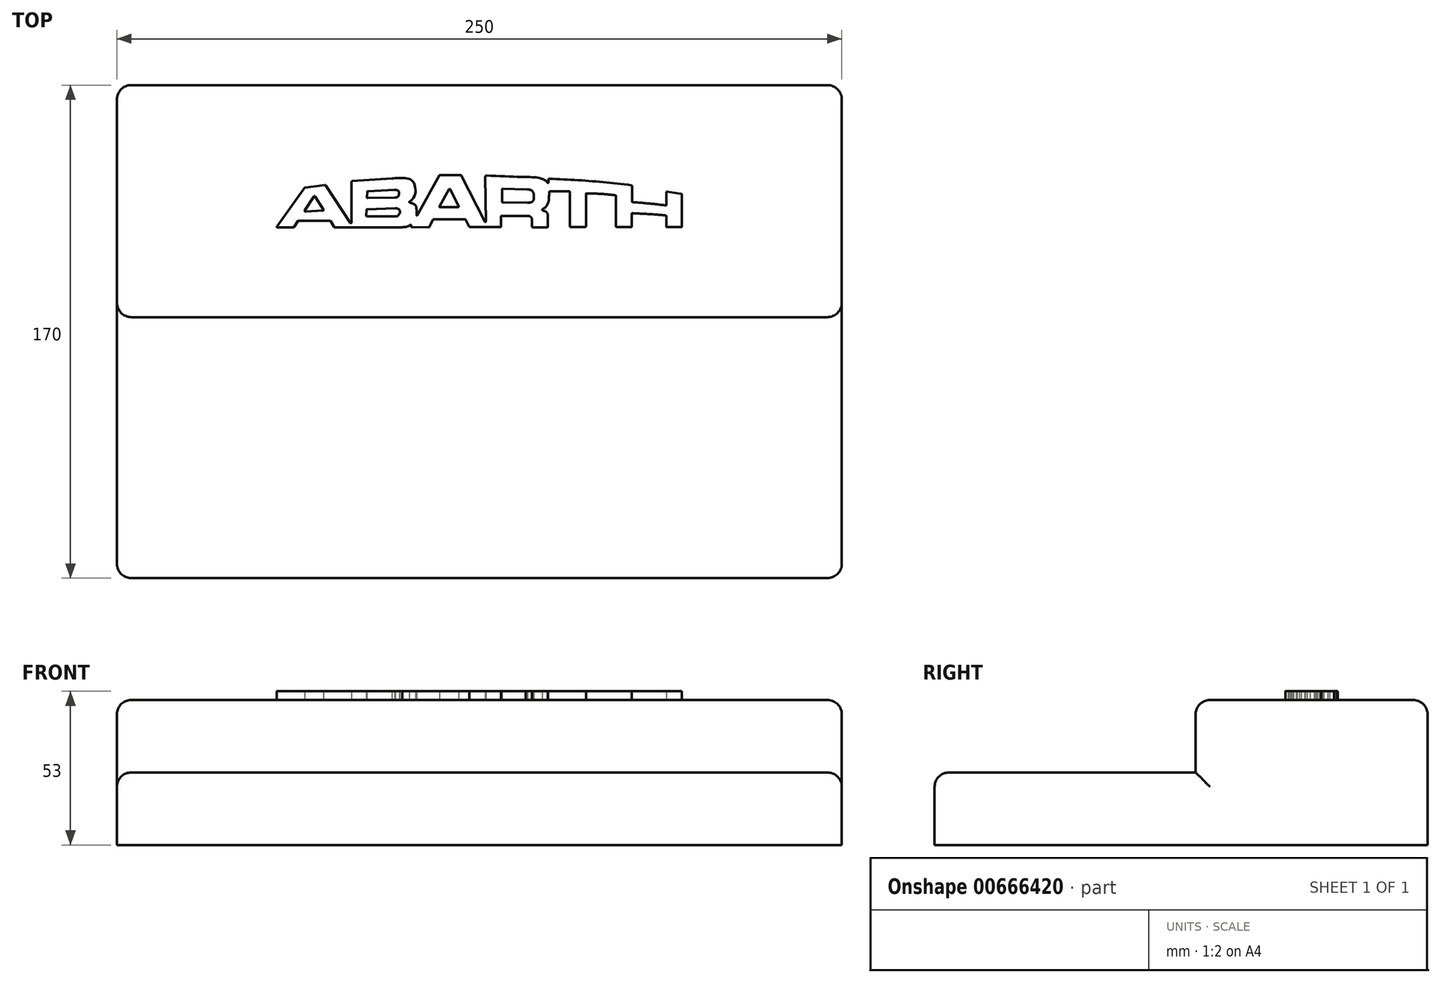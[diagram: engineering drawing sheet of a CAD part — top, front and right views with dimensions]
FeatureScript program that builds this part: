
annotation { "Feature Type Name" : "Feature", "Feature Type Description" : "" }
export const myFeature = defineFeature(function(context is Context, id is Id, definition is map)
    precondition{}
    {
        {
            var Q0;
            Q0=qCreatedBy(makeId("Top.planeOp"),FACE);
            var sketch = newSketch(context, id + "F0", { "sketchPlane" : qUnion([Q0])});
            skLineSegment(sketch, "E0.bottom", {"start": v(125, -40) * mm, "end": v(-125, -40) * mm});
            skLineSegment(sketch, "E0.top", {"start": v(125, 40) * mm, "end": v(-125, 40) * mm});
            skLineSegment(sketch, "E0.left", {"start": v(125, -40) * mm, "end": v(125, 40) * mm});
            skLineSegment(sketch, "E0.right", {"start": v(-125, -40) * mm, "end": v(-125, 40) * mm});
            skPoint(sketch, "E0.middle", {"position": v(0, 0) * mm});
            skSolve(sketch);
        }
        {
            var Q0;
            Q0=makeQuery(id+"F0.imprint","IMPRINT",FACE,{"disambiguationData":[TD([[makeQuery(id+"F0.imprint","IMPRINT",EDGE,{"derivedFrom":sQuery(id+"F0.wireOp",EDGE,"E0.bottom")}),-1.0]])]});
            extrude(context, id + "F1", {"entities" : qUnion([Q0]), "depth" : 25 * mm, "offsetDistance" : 25 * mm});
        }
        {
            var Q0;
            Q0=makeQuery(id+"F1.opExtrude","CAP_FACE",FACE,{"disambiguationData":[OSD([sQuery(id+"F0.wireOp",EDGE,"E0.bottom"),sQuery(id+"F0.wireOp",EDGE,"E0.top"),sQuery(id+"F0.wireOp",EDGE,"E0.left"),sQuery(id+"F0.wireOp",EDGE,"E0.right")])],"isStart":false});
            var sketch = newSketch(context, id + "F2", { "sketchPlane" : qUnion([Q0])});
            skLineSegment(sketch, "E1", {"start": v(-69.64, -9.06) * mm, "end": v(-64.06, -9.06) * mm});
            skLineSegment(sketch, "E2", {"start": v(-63.89, -8.97) * mm, "end": v(-62.5, -6.84) * mm});
            skLineSegment(sketch, "E3", {"start": v(-62.33, -6.75) * mm, "end": v(-51.48, -6.75) * mm});
            skLineSegment(sketch, "E4", {"start": v(-51.3, -6.84) * mm, "end": v(-50.02, -8.94) * mm});
            skLineSegment(sketch, "E5", {"start": v(-49.85, -9.04) * mm, "end": v(-26.5, -9) * mm});
            skLineSegment(sketch, "E6", {"start": v(-23.3, -8.96) * mm, "end": v(-17.46, -9.05) * mm});
            skLineSegment(sketch, "E7", {"start": v(-17.28, -8.95) * mm, "end": v(-15.84, -6.3) * mm});
            skLineSegment(sketch, "E8", {"start": v(-15.75, -6.24) * mm, "end": v(-4.93, -6.24) * mm});
            skLineSegment(sketch, "E9", {"start": v(-4.75, -6.35) * mm, "end": v(-3.41, -9) * mm});
            skLineSegment(sketch, "E10", {"start": v(-3.41, -9) * mm, "end": v(7.3, -8.99) * mm});
            skLineSegment(sketch, "E11", {"start": v(7.5, -8.79) * mm, "end": v(7.49, -5.27) * mm});
            skLineSegment(sketch, "E12", {"start": v(7.69, -5.07) * mm, "end": v(15.94, -5.07) * mm});
            skLineSegment(sketch, "E13", {"start": v(18.18, -6.73) * mm, "end": v(18.18, -8.82) * mm});
            skLineSegment(sketch, "E14", {"start": v(18.38, -9.02) * mm, "end": v(23.46, -9.02) * mm});
            skLineSegment(sketch, "E15", {"start": v(23.66, -8.82) * mm, "end": v(23.66, -5.07) * mm});
            skLineSegment(sketch, "E16", {"start": v(31.26, 3.12) * mm, "end": v(31.26, -8.71) * mm});
            skLineSegment(sketch, "E17", {"start": v(31.46, -8.91) * mm, "end": v(36.56, -8.91) * mm});
            skLineSegment(sketch, "E18", {"start": v(36.76, -8.71) * mm, "end": v(36.76, 2.47) * mm});
            skLineSegment(sketch, "E19", {"start": v(47.1, 1.82) * mm, "end": v(47.11, -8.74) * mm});
            skLineSegment(sketch, "E20", {"start": v(47.31, -8.94) * mm, "end": v(52.37, -8.94) * mm});
            skLineSegment(sketch, "E21", {"start": v(52.57, -8.74) * mm, "end": v(52.57, -4.38) * mm});
            skLineSegment(sketch, "E22", {"start": v(64.52, -5.17) * mm, "end": v(64.53, -8.78) * mm});
            skLineSegment(sketch, "E23", {"start": v(64.73, -8.98) * mm, "end": v(69.68, -8.98) * mm});
            skLineSegment(sketch, "E24", {"start": v(69.88, -8.78) * mm, "end": v(69.88, 2.26) * mm});
            skLineSegment(sketch, "E25", {"start": v(69.7, 2.46) * mm, "end": v(64.77, 3.25) * mm});
            skLineSegment(sketch, "E26", {"start": v(64.54, 3.05) * mm, "end": v(64.54, -1.3) * mm});
            skLineSegment(sketch, "E27", {"start": v(52.64, -0.15) * mm, "end": v(52.64, 5.27) * mm});
            skPoint(sketch, "E28.1.internal.snap0", {"position": v(58.57, -0.93) * mm});
            skFitSpline(sketch, "E28", {"points": [v(52.75, -0.34) * mm, v(59.5, -0.93) * mm, v(64.4, -1.5) * mm], "startDerivative": vector(13.02, -1.03) * mm, "endDerivative": vector(10.2, -1.3) * mm});
            skFitSpline(sketch, "E29", {"points": [v(64.42, -4.98) * mm, v(60.34, -4.58) * mm, v(55.98, -4.34) * mm, v(52.7, -4.18) * mm], "startDerivative": vector(-11.7, 1.26) * mm, "endDerivative": vector(-10.29, 0.51) * mm});
            skFitSpline(sketch, "E30", {"points": [v(36.88, 2.68) * mm, v(42.24, 2.46) * mm, v(47, 2.01) * mm], "startDerivative": vector(10.58, -0.3) * mm, "endDerivative": vector(9.64, -1.04) * mm});
            skFitSpline(sketch, "E31", {"points": [v(52.52, 5.46) * mm, v(38.45, 6.9) * mm, v(23.98, 7.7) * mm], "startDerivative": vector(-28.22, 3.11) * mm, "endDerivative": vector(-28.88, 1.38) * mm});
            skLineSegment(sketch, "E32", {"start": v(24.28, 3.32) * mm, "end": v(31.06, 3.32) * mm});
            skLineSegment(sketch, "E33", {"start": v(-6.23, 8.9) * mm, "end": v(1.9, -7.08) * mm});
            skLineSegment(sketch, "E34", {"start": v(2.07, 8.37) * mm, "end": v(2.27, -6.99) * mm});
            skLineSegment(sketch, "E35", {"start": v(-13.5, 9.02) * mm, "end": v(-6.4, 9) * mm});
            skLineSegment(sketch, "E36", {"start": v(-13.68, 8.92) * mm, "end": v(-21.48, -4.95) * mm});
            skLineSegment(sketch, "E37", {"start": v(-69.8, -8.74) * mm, "end": v(-60.27, 4.59) * mm});
            skLineSegment(sketch, "E38", {"start": v(-60.13, 4.67) * mm, "end": v(-53.17, 5.56) * mm});
            skLineSegment(sketch, "E39", {"start": v(-52.98, 5.47) * mm, "end": v(-44.42, -7.51) * mm});
            skLineSegment(sketch, "E40", {"start": v(-44.05, -7.4) * mm, "end": v(-44.05, 6.67) * mm});
            skLineSegment(sketch, "E41", {"start": v(-43.87, 6.87) * mm, "end": v(-30.13, 7.83) * mm});
            skLineSegment(sketch, "E42", {"start": v(-23.5, -8.77) * mm, "end": v(-23.5, -8.37) * mm});
            skFitSpline(sketch, "E43", {"points": [v(-23.7, -8.13) * mm, v(-24.5, -8.62) * mm, v(-25.52, -8.94) * mm, v(-26.5, -9) * mm], "startDerivative": vector(-2.31, -1.62) * mm, "endDerivative": vector(-2.91, -0.1) * mm});
            skFitSpline(sketch, "E44", {"points": [v(-21.67, -5.2) * mm, v(-21.66, -3.24) * mm, v(-21.74, -2.03) * mm, v(-22.12, -1.33) * mm, v(-23.2, -0.73) * mm, v(-24.06, -0.6) * mm], "startDerivative": vector(0.06, 7.93) * mm, "endDerivative": vector(-4.73, 0.3) * mm});
            skFitSpline(sketch, "E45", {"points": [v(-24.13, -0.1) * mm, v(-23.14, 0.54) * mm, v(-22.14, 2.46) * mm, v(-22.12, 4.53) * mm, v(-22.65, 6.42) * mm, v(-23.83, 7.5) * mm, v(-25.3, 7.9) * mm, v(-28.37, 7.93) * mm, v(-30.13, 7.83) * mm], "startDerivative": vector(10.17, 4.79) * mm, "endDerivative": vector(-13.04, -0.76) * mm});
            skFitSpline(sketch, "E46", {"points": [v(2.4, 8.78) * mm, v(16.04, 8.3) * mm, v(20.13, 8.07) * mm, v(22.39, 7.37) * mm, v(23.23, 6.73) * mm, v(23.65, 6.14) * mm], "startDerivative": vector(38.58, -1.46) * mm, "endDerivative": vector(4.08, -6.44) * mm});
            skFitSpline(sketch, "E47", {"points": [v(24.08, 3.2) * mm, v(24, 0.71) * mm, v(23.66, -0.8) * mm, v(22.61, -2.27) * mm, v(21.75, -2.78) * mm], "startDerivative": vector(-0.22, -8.68) * mm, "endDerivative": vector(-4.38, -1.91) * mm});
            skFitSpline(sketch, "E48", {"points": [v(18.18, -6.73) * mm, v(18.07, -5.9) * mm, v(17.47, -5.26) * mm, v(16.6, -5.1) * mm, v(15.94, -5.07) * mm], "startDerivative": vector(0, 3.34) * mm, "endDerivative": vector(-2.8, 0.11) * mm});
            skFitSpline(sketch, "E49", {"points": [v(23.66, -5.07) * mm, v(23.6, -4.53) * mm, v(23.33, -4) * mm, v(22.8, -3.56) * mm, v(22, -3.3) * mm, v(21.8, -3.27) * mm], "startDerivative": vector(-0.2, 2.72) * mm, "endDerivative": vector(-1.34, 0.14) * mm});
            skLineSegment(sketch, "E50", {"start": v(23.85, 7.5) * mm, "end": v(23.88, 6.47) * mm});
            skArc(sketch, "E51.filletArc", {"start": v(-69.8, -8.74) * mm, "mid": v(-69.82, -8.95) * mm, "end": v(-69.64, -9.06) * mm});
            skArc(sketch, "E52.filletArc", {"start": v(-64.06, -9.06) * mm, "mid": v(-63.96, -9.03) * mm, "end": v(-63.89, -8.97) * mm});
            skArc(sketch, "E53.filletArc", {"start": v(-62.33, -6.75) * mm, "mid": v(-62.42, -6.77) * mm, "end": v(-62.5, -6.84) * mm});
            skArc(sketch, "E54.filletArc", {"start": v(-51.3, -6.84) * mm, "mid": v(-51.38, -6.77) * mm, "end": v(-51.48, -6.75) * mm});
            skArc(sketch, "E55.filletArc", {"start": v(-50.02, -8.94) * mm, "mid": v(-49.95, -9.01) * mm, "end": v(-49.85, -9.04) * mm});
            skArc(sketch, "E56.filletArc", {"start": v(-52.98, 5.47) * mm, "mid": v(-53.06, 5.54) * mm, "end": v(-53.17, 5.56) * mm});
            skPoint(sketch, "E57.visualSharp", {"position": v(-60.22, 4.66) * mm});
            skArc(sketch, "E57.filletArc", {"start": v(-60.13, 4.67) * mm, "mid": v(-60.2, 4.64) * mm, "end": v(-60.27, 4.59) * mm});
            skArc(sketch, "E58.filletArc", {"start": v(-43.87, 6.87) * mm, "mid": v(-44, 6.8) * mm, "end": v(-44.05, 6.67) * mm});
            skArc(sketch, "E59.filletArc", {"start": v(-17.46, -9.05) * mm, "mid": v(-17.36, -9.02) * mm, "end": v(-17.28, -8.95) * mm});
            skArc(sketch, "E60.filletArc", {"start": v(-23.5, -8.77) * mm, "mid": v(-23.44, -8.9) * mm, "end": v(-23.3, -8.96) * mm});
            skArc(sketch, "E61.filletArc", {"start": v(-15.75, -6.24) * mm, "mid": v(-15.8, -6.25) * mm, "end": v(-15.84, -6.3) * mm});
            skArc(sketch, "E62.filletArc", {"start": v(-4.75, -6.35) * mm, "mid": v(-4.82, -6.27) * mm, "end": v(-4.93, -6.24) * mm});
            skLineSegment(sketch, "E63.filletArc", {"start": v(-63.23, 51.31) * mm, "end": v(-63.23, 51.31) * mm});
            skArc(sketch, "E64.filletArc", {"start": v(7.3, -8.99) * mm, "mid": v(7.44, -8.93) * mm, "end": v(7.5, -8.79) * mm});
            skArc(sketch, "E65.filletArc", {"start": v(7.69, -5.07) * mm, "mid": v(7.55, -5.13) * mm, "end": v(7.49, -5.27) * mm});
            skArc(sketch, "E66.filletArc", {"start": v(18.18, -8.82) * mm, "mid": v(18.24, -8.96) * mm, "end": v(18.38, -9.02) * mm});
            skArc(sketch, "E67.filletArc", {"start": v(23.46, -9.02) * mm, "mid": v(23.6, -8.96) * mm, "end": v(23.66, -8.82) * mm});
            skArc(sketch, "E68.filletArc", {"start": v(24.28, 3.32) * mm, "mid": v(24.14, 3.26) * mm, "end": v(24.08, 3.12) * mm});
            skArc(sketch, "E69.filletArc", {"start": v(31.26, 3.12) * mm, "mid": v(31.2, 3.26) * mm, "end": v(31.06, 3.32) * mm});
            skArc(sketch, "E70.filletArc", {"start": v(31.26, -8.71) * mm, "mid": v(31.32, -8.85) * mm, "end": v(31.46, -8.91) * mm});
            skArc(sketch, "E71.filletArc", {"start": v(36.56, -8.91) * mm, "mid": v(36.7, -8.85) * mm, "end": v(36.76, -8.71) * mm});
            skArc(sketch, "E72.filletArc", {"start": v(36.96, 2.67) * mm, "mid": v(36.82, 2.62) * mm, "end": v(36.76, 2.47) * mm});
            skArc(sketch, "E73.filletArc", {"start": v(47.1, 1.82) * mm, "mid": v(47.05, 1.95) * mm, "end": v(46.93, 2.02) * mm});
            skArc(sketch, "E74.filletArc", {"start": v(47.11, -8.74) * mm, "mid": v(47.17, -8.89) * mm, "end": v(47.31, -8.94) * mm});
            skArc(sketch, "E75.filletArc", {"start": v(52.37, -8.94) * mm, "mid": v(52.51, -8.89) * mm, "end": v(52.57, -8.74) * mm});
            skArc(sketch, "E76.filletArc", {"start": v(52.78, -4.18) * mm, "mid": v(52.64, -4.24) * mm, "end": v(52.57, -4.38) * mm});
            skArc(sketch, "E77.filletArc", {"start": v(64.53, -8.78) * mm, "mid": v(64.59, -8.92) * mm, "end": v(64.73, -8.98) * mm});
            skArc(sketch, "E78.filletArc", {"start": v(64.52, -5.17) * mm, "mid": v(64.47, -5.04) * mm, "end": v(64.35, -4.97) * mm});
            skArc(sketch, "E79.filletArc", {"start": v(69.68, -8.98) * mm, "mid": v(69.82, -8.92) * mm, "end": v(69.88, -8.78) * mm});
            skArc(sketch, "E80.filletArc", {"start": v(69.88, 2.26) * mm, "mid": v(69.83, 2.39) * mm, "end": v(69.7, 2.46) * mm});
            skArc(sketch, "E81.filletArc", {"start": v(64.77, 3.25) * mm, "mid": v(64.6, 3.2) * mm, "end": v(64.54, 3.05) * mm});
            skArc(sketch, "E82.filletArc", {"start": v(64.31, -1.5) * mm, "mid": v(64.47, -1.45) * mm, "end": v(64.54, -1.3) * mm});
            skArc(sketch, "E83.filletArc", {"start": v(52.64, -0.15) * mm, "mid": v(52.69, -0.29) * mm, "end": v(52.82, -0.35) * mm});
            skArc(sketch, "E84.filletArc", {"start": v(52.64, 5.27) * mm, "mid": v(52.59, 5.4) * mm, "end": v(52.46, 5.47) * mm});
            skArc(sketch, "E85.filletArc", {"start": v(24.06, 7.7) * mm, "mid": v(23.9, 7.65) * mm, "end": v(23.85, 7.5) * mm});
            skArc(sketch, "E86.filletArc", {"start": v(2.48, 8.78) * mm, "mid": v(2.19, 8.66) * mm, "end": v(2.07, 8.37) * mm});
            skPoint(sketch, "E87.visualSharp", {"position": v(-6.28, 9) * mm});
            skArc(sketch, "E87.filletArc", {"start": v(-6.23, 8.9) * mm, "mid": v(-6.3, 8.97) * mm, "end": v(-6.4, 9) * mm});
            skArc(sketch, "E88.filletArc", {"start": v(-13.5, 9.02) * mm, "mid": v(-13.6, 9) * mm, "end": v(-13.68, 8.92) * mm});
            skArc(sketch, "E89.filletArc", {"start": v(-44.42, -7.51) * mm, "mid": v(-44.2, -7.6) * mm, "end": v(-44.05, -7.4) * mm});
            skArc(sketch, "E90.filletArc", {"start": v(-21.67, -4.9) * mm, "mid": v(-21.6, -5) * mm, "end": v(-21.48, -4.95) * mm});
            skArc(sketch, "E91.filletArc", {"start": v(1.9, -7.08) * mm, "mid": v(2.12, -7.18) * mm, "end": v(2.27, -6.99) * mm});
            skArc(sketch, "E92.filletArc", {"start": v(-23.5, -8.37) * mm, "mid": v(-23.61, -8.2) * mm, "end": v(-23.82, -8.2) * mm});
            skArc(sketch, "E93.filletArc", {"start": v(23.51, 6.35) * mm, "mid": v(23.74, 6.27) * mm, "end": v(23.88, 6.47) * mm});
            skArc(sketch, "E94.filletArc", {"start": v(-23.93, -0.01) * mm, "mid": v(-24.1, -0.36) * mm, "end": v(-23.82, -0.61) * mm});
            skArc(sketch, "E95.filletArc", {"start": v(21.93, -2.7) * mm, "mid": v(21.75, -3.02) * mm, "end": v(22, -3.3) * mm});
            skLineSegment(sketch, "E96", {"start": v(-59.98, -3.56) * mm, "end": v(-53.93, -3.28) * mm});
            skLineSegment(sketch, "E97", {"start": v(-53.77, -2.97) * mm, "end": v(-56.66, 1.61) * mm});
            skLineSegment(sketch, "E98", {"start": v(-57, 1.61) * mm, "end": v(-60.16, -3.25) * mm});
            skLineSegment(sketch, "E99", {"start": v(-13.55, -2.12) * mm, "end": v(-7.31, -2.12) * mm});
            skLineSegment(sketch, "E100", {"start": v(-7.14, -1.83) * mm, "end": v(-10.08, 4.08) * mm});
            skLineSegment(sketch, "E101", {"start": v(-10.43, 4.09) * mm, "end": v(-13.72, -1.82) * mm});
            skLineSegment(sketch, "E102", {"start": v(7.82, 4.03) * mm, "end": v(7.82, -0.23) * mm});
            skLineSegment(sketch, "E103", {"start": v(8.02, -0.43) * mm, "end": v(16.64, -0.53) * mm});
            skLineSegment(sketch, "E104", {"start": v(16.49, 4.03) * mm, "end": v(8.03, 4.23) * mm});
            skLineSegment(sketch, "E105", {"start": v(18.78, 2.1) * mm, "end": v(18.78, 0.85) * mm});
            skFitSpline(sketch, "E106", {"points": [v(16.49, 4.03) * mm, v(17.65, 3.85) * mm, v(18.44, 3.3) * mm, v(18.76, 2.56) * mm, v(18.78, 2.1) * mm], "startDerivative": vector(4.08, -0.25) * mm, "endDerivative": vector(-0.06, -2.33) * mm});
            skFitSpline(sketch, "E107", {"points": [v(18.78, 0.85) * mm, v(18.75, 0.44) * mm, v(18.34, -0.14) * mm, v(17.52, -0.48) * mm, v(16.64, -0.53) * mm], "startDerivative": vector(0.06, -2.04) * mm, "endDerivative": vector(-3.14, 0) * mm});
            skLineSegment(sketch, "E108", {"start": v(-38.67, 3.2) * mm, "end": v(-38.75, 1.26) * mm});
            skLineSegment(sketch, "E109", {"start": v(-38.48, 3.4) * mm, "end": v(-29.2, 3.85) * mm});
            skLineSegment(sketch, "E110", {"start": v(-29.17, 1.19) * mm, "end": v(-38.55, 1.05) * mm});
            skLineSegment(sketch, "E111", {"start": v(-28.93, -2.45) * mm, "end": v(-38.73, -2.79) * mm});
            skLineSegment(sketch, "E112", {"start": v(-28.99, -5.23) * mm, "end": v(-38.8, -5.21) * mm});
            skFitSpline(sketch, "E113", {"points": [v(-29.2, 3.85) * mm, v(-28.27, 3.74) * mm, v(-27.78, 3.28) * mm, v(-27.64, 2.65) * mm, v(-27.8, 1.95) * mm, v(-28.19, 1.46) * mm, v(-28.54, 1.24) * mm, v(-28.87, 1.19) * mm, v(-29.17, 1.19) * mm], "startDerivative": vector(6.28, 0.05) * mm, "endDerivative": vector(-3.3, 0.32) * mm});
            skFitSpline(sketch, "E114", {"points": [v(-28.99, -5.23) * mm, v(-28.29, -5.18) * mm, v(-27.72, -4.7) * mm, v(-27.37, -3.67) * mm, v(-27.75, -2.83) * mm, v(-28.4, -2.5) * mm, v(-28.93, -2.45) * mm], "startDerivative": vector(4.62, -0.21) * mm, "endDerivative": vector(-3.8, 0.08) * mm});
            skLineSegment(sketch, "E115.trimOffspring", {"start": v(-38.92, -2.98) * mm, "end": v(-39, -5) * mm});
            skPoint(sketch, "E116.visualSharp", {"position": v(-56.82, 1.87) * mm});
            skArc(sketch, "E116.filletArc", {"start": v(-56.66, 1.61) * mm, "mid": v(-56.82, 1.7) * mm, "end": v(-57, 1.61) * mm});
            skPoint(sketch, "E117.visualSharp", {"position": v(-53.58, -3.26) * mm});
            skArc(sketch, "E117.filletArc", {"start": v(-53.93, -3.28) * mm, "mid": v(-53.76, -3.17) * mm, "end": v(-53.77, -2.97) * mm});
            skPoint(sketch, "E118.visualSharp", {"position": v(-60.37, -3.58) * mm});
            skArc(sketch, "E118.filletArc", {"start": v(-60.16, -3.25) * mm, "mid": v(-60.16, -3.46) * mm, "end": v(-59.98, -3.56) * mm});
            skPoint(sketch, "E119.visualSharp", {"position": v(-10.25, 4.42) * mm});
            skArc(sketch, "E119.filletArc", {"start": v(-10.08, 4.08) * mm, "mid": v(-10.25, 4.19) * mm, "end": v(-10.43, 4.09) * mm});
            skPoint(sketch, "E120.visualSharp", {"position": v(-13.9, -2.12) * mm});
            skArc(sketch, "E120.filletArc", {"start": v(-13.72, -1.82) * mm, "mid": v(-13.72, -2.02) * mm, "end": v(-13.55, -2.12) * mm});
            skPoint(sketch, "E121.visualSharp", {"position": v(-7, -2.12) * mm});
            skArc(sketch, "E121.filletArc", {"start": v(-7.31, -2.12) * mm, "mid": v(-7.14, -2.02) * mm, "end": v(-7.14, -1.83) * mm});
            skPoint(sketch, "E122.visualSharp", {"position": v(7.82, 4.24) * mm});
            skArc(sketch, "E122.filletArc", {"start": v(8.03, 4.23) * mm, "mid": v(7.88, 4.17) * mm, "end": v(7.82, 4.03) * mm});
            skPoint(sketch, "E123.visualSharp", {"position": v(7.82, -0.42) * mm});
            skArc(sketch, "E123.filletArc", {"start": v(7.82, -0.23) * mm, "mid": v(7.88, -0.37) * mm, "end": v(8.02, -0.43) * mm});
            skPoint(sketch, "E124.visualSharp", {"position": v(-38.67, 3.4) * mm});
            skArc(sketch, "E124.filletArc", {"start": v(-38.48, 3.4) * mm, "mid": v(-38.61, 3.34) * mm, "end": v(-38.67, 3.2) * mm});
            skPoint(sketch, "E125.visualSharp", {"position": v(-38.76, 1.05) * mm});
            skArc(sketch, "E125.filletArc", {"start": v(-38.75, 1.26) * mm, "mid": v(-38.7, 1.12) * mm, "end": v(-38.55, 1.05) * mm});
            skPoint(sketch, "E126.visualSharp", {"position": v(-38.91, -2.8) * mm});
            skArc(sketch, "E126.filletArc", {"start": v(-38.73, -2.79) * mm, "mid": v(-38.86, -2.84) * mm, "end": v(-38.92, -2.98) * mm});
            skPoint(sketch, "E127.visualSharp", {"position": v(-39, -5.21) * mm});
            skArc(sketch, "E127.filletArc", {"start": v(-39, -5) * mm, "mid": v(-38.94, -5.15) * mm, "end": v(-38.8, -5.21) * mm});
            skLineSegment(sketch, "E128", {"start": v(-81, 0) * mm, "end": v(81, 0) * mm, "construction": true});
            skLineSegment(sketch, "E129", {"start": v(0, 13.76) * mm, "end": v(0, -13.76) * mm, "construction": true});
            skPoint(sketch, "E130.middle", {"position": v(0, 0) * mm});
            skSolve(sketch);
        }
        {
            var Q0;
            Q0 = qSketchRegion(id + "F2", true);
            extrude(context, id + "F3", {"entities" : qUnion([Q0]), "operationType" : NewBodyOperationType.ADD, "depth" : 3 * mm, "offsetDistance" : 25 * mm});
        }
        {
            var Q0;
            Q0=makeQuery(id+"F1.opExtrude","CAP_FACE",FACE,{"disambiguationData":[OSD([sQuery(id+"F0.wireOp",EDGE,"E0.bottom"),sQuery(id+"F0.wireOp",EDGE,"E0.top"),sQuery(id+"F0.wireOp",EDGE,"E0.left"),sQuery(id+"F0.wireOp",EDGE,"E0.right")])],"isStart":true});
            var sketch = newSketch(context, id + "F4", { "sketchPlane" : qUnion([Q0])});
            skLineSegment(sketch, "E131.bottom", {"start": v(-125, -40) * mm, "end": v(125, -40) * mm});
            skLineSegment(sketch, "E131.top", {"start": v(-125, 130) * mm, "end": v(125, 130) * mm});
            skLineSegment(sketch, "E131.left", {"start": v(-125, -40) * mm, "end": v(-125, 130) * mm});
            skLineSegment(sketch, "E131.right", {"start": v(125, -40) * mm, "end": v(125, 130) * mm});
            skSolve(sketch);
        }
        {
            var Q0;
            {var subQ0=sQuery(id+"F4.wireOp",EDGE,"E131.top");Q0=makeQuery(id+"F4.imprint","IMPRINT",FACE,{"disambiguationData":[TD([[makeQuery(id+"F4.imprint","IMPRINT",EDGE,{"derivedFrom":subQ0}),-1.0]])]});}
            var Q1;
            {var subQ0=sQuery(id+"F4.wireOp",EDGE,"E131.bottom");Q1=makeQuery(id+"F4.imprint","IMPRINT",FACE,{"disambiguationData":[TD([[makeQuery(id+"F4.imprint","IMPRINT",EDGE,{"derivedFrom":subQ0}),-1.0]])]});}
            extrude(context, id + "F5", {"entities" : qUnion([Q0, Q1]), "operationType" : NewBodyOperationType.ADD, "depth" : 25 * mm, "offsetDistance" : 25 * mm});
        }
        {
            var Q0;
            Q0=makeQuery(id+"F1.opExtrude","CAP_EDGE",EDGE,{"disambiguationData":[OSD([sQuery(id+"F0.wireOp",EDGE,"E0.bottom")])],"isStart":false});
            var Q1;
            Q1=makeQuery(id+"F1.opExtrude","CAP_EDGE",EDGE,{"disambiguationData":[OSD([sQuery(id+"F0.wireOp",EDGE,"E0.left")])],"isStart":false});
            var Q2;
            Q2=makeQuery(id+"F1.opExtrude","CAP_EDGE",EDGE,{"disambiguationData":[OSD([sQuery(id+"F0.wireOp",EDGE,"E0.right")])],"isStart":false});
            var Q3;
            Q3=makeQuery(id+"F1.opExtrude","CAP_EDGE",EDGE,{"disambiguationData":[OSD([sQuery(id+"F0.wireOp",EDGE,"E0.top")])],"isStart":false});
            var Q4;
            Q4=makeQuery(id+"F5.boolean.opBoolean","MERGE",EDGE,{"derivedFrom":[makeQuery(id+"F1.opExtrude","SWEPT_EDGE",EDGE,{"disambiguationData":[OSD([sQuery(id+"F0.wireOp",EDGE,"E0.top"),sQuery(id+"F0.wireOp",EDGE,"E0.left")])]}),makeQuery(id+"F5.opExtrude","SWEPT_EDGE",EDGE,{"disambiguationData":[OSD([sQuery(id+"F4.wireOp",EDGE,"E131.bottom"),sQuery(id+"F4.wireOp",EDGE,"E131.right")])]})]});
            var Q5;
            Q5=makeQuery(id+"F1.opExtrude","SWEPT_EDGE",EDGE,{"disambiguationData":[OSD([sQuery(id+"F0.wireOp",EDGE,"E0.bottom"),sQuery(id+"F0.wireOp",EDGE,"E0.left")])]});
            var Q6;
            Q6=makeQuery(id+"F5.opExtrude","CAP_EDGE",EDGE,{"disambiguationData":[OSD([sQuery(id+"F4.wireOp",EDGE,"E131.right")])],"isStart":true});
            var Q7;
            Q7=makeQuery(id+"F1.opExtrude","SWEPT_EDGE",EDGE,{"disambiguationData":[OSD([sQuery(id+"F0.wireOp",EDGE,"E0.bottom"),sQuery(id+"F0.wireOp",EDGE,"E0.right")])]});
            var Q8;
            Q8=makeQuery(id+"F5.opExtrude","CAP_EDGE",EDGE,{"disambiguationData":[OSD([sQuery(id+"F4.wireOp",EDGE,"E131.left")])],"isStart":true});
            var Q9;
            Q9=makeQuery(id+"F5.boolean.opBoolean","MERGE",EDGE,{"derivedFrom":[makeQuery(id+"F1.opExtrude","SWEPT_EDGE",EDGE,{"disambiguationData":[OSD([sQuery(id+"F0.wireOp",EDGE,"E0.top"),sQuery(id+"F0.wireOp",EDGE,"E0.right")])]}),makeQuery(id+"F5.opExtrude","SWEPT_EDGE",EDGE,{"disambiguationData":[OSD([sQuery(id+"F4.wireOp",EDGE,"E131.bottom"),sQuery(id+"F4.wireOp",EDGE,"E131.left")])]})]});
            var Q10;
            Q10=makeQuery(id+"F5.opExtrude","SWEPT_EDGE",EDGE,{"disambiguationData":[OSD([sQuery(id+"F4.wireOp",EDGE,"E131.top"),sQuery(id+"F4.wireOp",EDGE,"E131.left")])]});
            var Q11;
            Q11=makeQuery(id+"F5.opExtrude","CAP_EDGE",EDGE,{"disambiguationData":[OSD([sQuery(id+"F4.wireOp",EDGE,"E131.top")])],"isStart":true});
            var Q12;
            Q12=makeQuery(id+"F5.opExtrude","SWEPT_EDGE",EDGE,{"disambiguationData":[OSD([sQuery(id+"F4.wireOp",EDGE,"E131.top"),sQuery(id+"F4.wireOp",EDGE,"E131.right")])]});
            fillet(context, id + "F6", {"entities" : qUnion([Q0, Q1, Q2, Q3, Q4, Q5, Q6, Q7, Q8, Q9, Q10, Q11, Q12]), "radius" : 5 * mm, "tangentPropagation" : true, "allowEdgeOverflow" : false});
        }
    });
